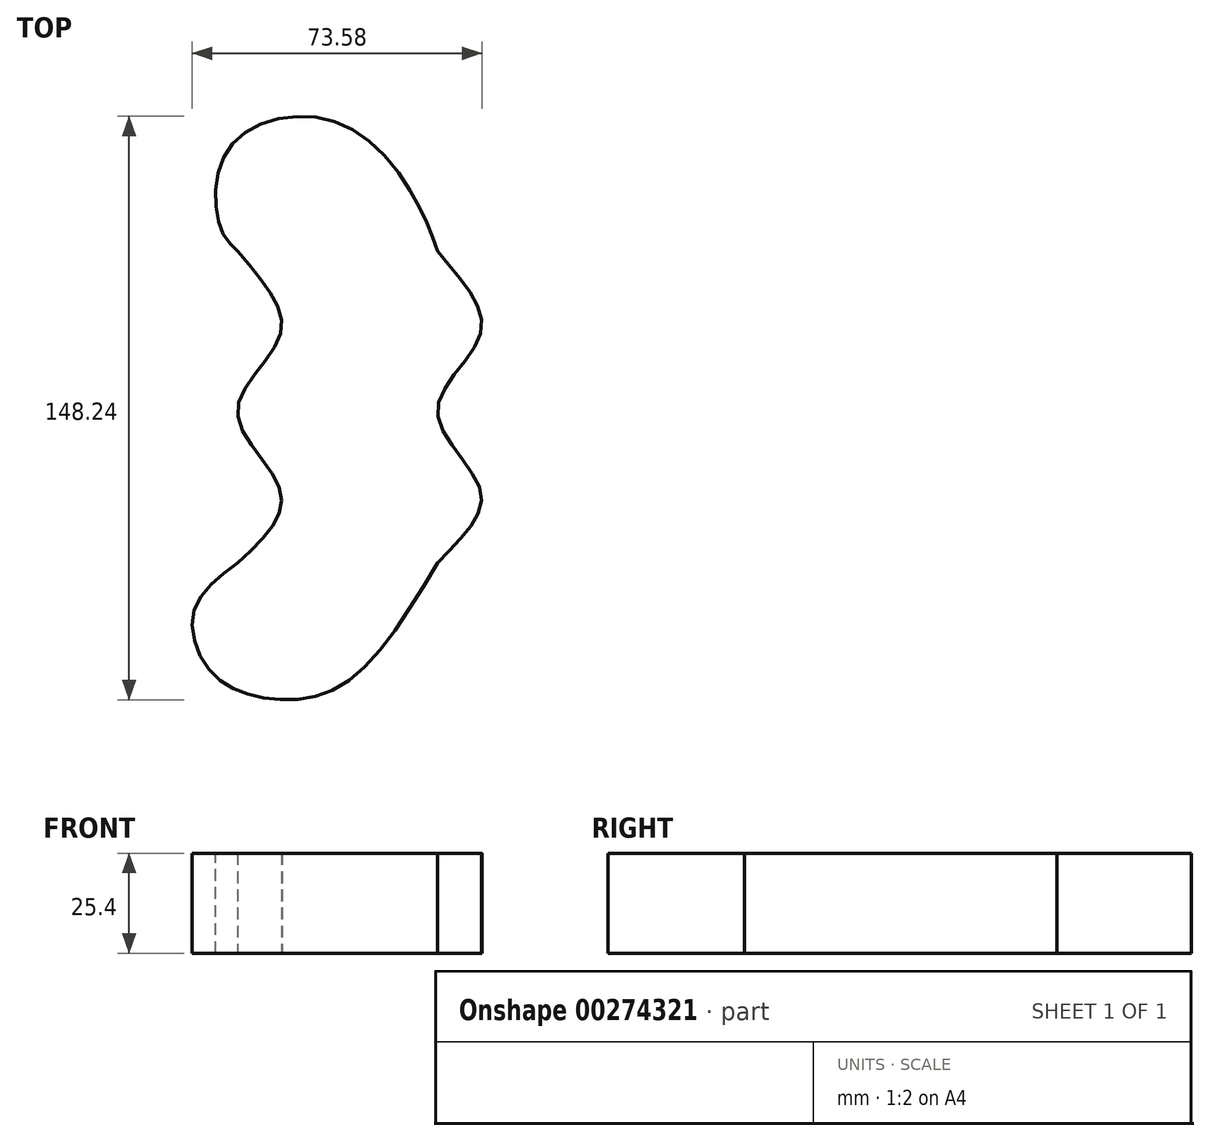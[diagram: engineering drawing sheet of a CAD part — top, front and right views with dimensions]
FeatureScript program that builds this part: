
annotation { "Feature Type Name" : "Feature", "Feature Type Description" : "" }
export const myFeature = defineFeature(function(context is Context, id is Id, definition is map)
    precondition{}
    {
        {
            var Q0;
            Q0=qCreatedBy(makeId("Top.planeOp"),FACE);
            var sketch = newSketch(context, id + "F0", { "sketchPlane" : qUnion([Q0])});
            skFitSpline(sketch, "E0", {"points": [v(-26.97, 55.88) * mm, v(-15.85, 35.56) * mm, v(-26.97, 15.12) * mm, v(-15.85, -5.9) * mm, v(-26.97, -23.41) * mm], "startDerivative": vector(65.22, -81.26) * mm, "endDerivative": vector(-76.31, -70.43) * mm});
            skFitSpline(sketch, "E1", {"points": [v(23.83, 55.88) * mm, v(34.95, 35.56) * mm, v(23.83, 15.12) * mm, v(34.95, -5.9) * mm, v(23.83, -23.41) * mm], "startDerivative": vector(64.07, -80.62) * mm, "endDerivative": vector(-65.95, -71.3) * mm});
            skPoint(sketch, "E2.endSnap0", {"position": v(-1.57, -23.41) * mm});
            skFitSpline(sketch, "E3", {"points": [v(-26.97, 55.88) * mm, v(-30.86, 60.64) * mm, v(-32.38, 72.26) * mm, v(-26.97, 84.45) * mm, v(-11.84, 90.05) * mm, v(5.43, 84.65) * mm, v(19.1, 67.39) * mm, v(23.83, 55.88) * mm], "startDerivative": vector(-45.4, 41.78) * mm, "endDerivative": vector(27.28, -79.34) * mm});
            skFitSpline(sketch, "E4", {"points": [v(23.83, -23.41) * mm, v(0, -54.16) * mm, v(-19.75, -57.76) * mm, v(-33.77, -50.92) * mm, v(-38.09, -35.82) * mm, v(-26.97, -23.41) * mm], "startDerivative": vector(-81.75, -137.12) * mm, "endDerivative": vector(81.71, 61.54) * mm});
            skSolve(sketch);
        }
        {
            var Q0;
            Q0=makeQuery(id+"F0.imprint","IMPRINT",FACE,{"disambiguationData":[TD([[makeQuery(id+"F0.imprint","IMPRINT",EDGE,{"derivedFrom":sQuery(id+"F0.wireOp",EDGE,"E0")}),1.0]])]});
            extrude(context, id + "F1", {"entities" : qUnion([Q0]), "depth" : 25.4 * mm});
        }
    });
